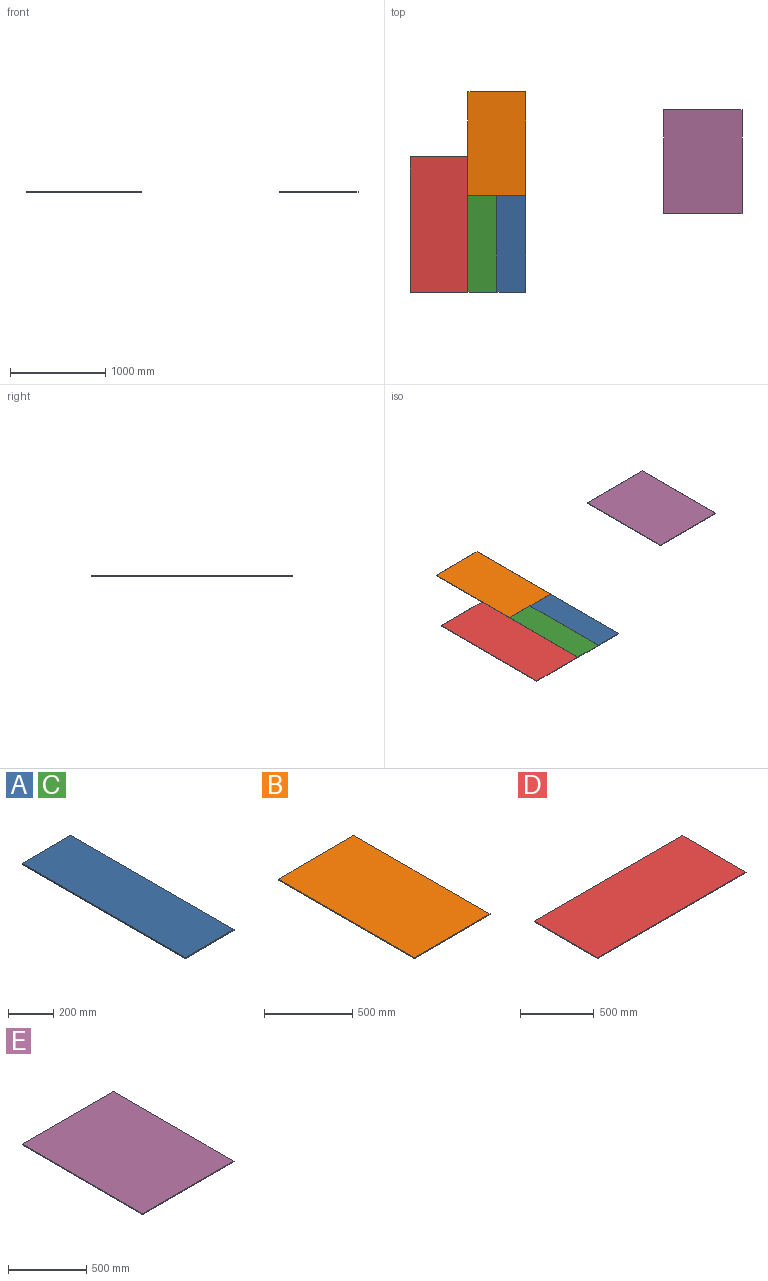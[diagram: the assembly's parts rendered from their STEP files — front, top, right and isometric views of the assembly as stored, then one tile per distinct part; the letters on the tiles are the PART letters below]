
ASSEMBLY  parts=5 mates=10
PART A: 6 faces, bbox 304.8x1016x6.4 mm
  f0: plane 304.8x6.35mm, normal (0,-1,0), area 1935.5mm2, adj f1,f3,f4,f5
  f1: plane 1016x6.35mm, normal (1,0,0), area 6451.6mm2, adj f0,f2,f4,f5
  f2: plane 304.8x6.35mm, normal (0,1,0), area 1935.5mm2, adj f1,f3,f4,f5
  f3: plane 1016x6.35mm, normal (-1,0,0), area 6451.6mm2, adj f0,f2,f4,f5
  f4: plane 1016x304.8mm, normal (0,0,1), area 309676.8mm2, adj f0,f1,f2,f3
  f5: plane 1016x304.8mm, normal (0,0,-1), area 309676.8mm2, adj f0,f1,f2,f3
PART B: 6 faces, bbox 609.6x1092.2x6.4 mm
  f0: plane 609.6x6.35mm, normal (0,-1,0), area 3871mm2, adj f1,f3,f4,f5
  f1: plane 1092.2x6.35mm, normal (1,0,0), area 6935.5mm2, adj f0,f2,f4,f5
  f2: plane 609.6x6.35mm, normal (0,1,0), area 3871mm2, adj f1,f3,f4,f5
  f3: plane 1092.2x6.35mm, normal (-1,0,0), area 6935.5mm2, adj f0,f2,f4,f5
  f4: plane 1092.2x609.6mm, normal (0,0,1), area 665805.1mm2, adj f0,f1,f2,f3
  f5: plane 1092.2x609.6mm, normal (0,0,-1), area 665805.1mm2, adj f0,f1,f2,f3
PART C: same geometry as A
PART D: 6 faces, bbox 1422.4x609.6x6.4 mm
  f0: plane 1422.4x6.35mm, normal (0,-1,0), area 9032.2mm2, adj f1,f3,f4,f5
  f1: plane 609.6x6.35mm, normal (1,0,0), area 3871mm2, adj f0,f2,f4,f5
  f2: plane 1422.4x6.35mm, normal (0,1,0), area 9032.2mm2, adj f1,f3,f4,f5
  f3: plane 609.6x6.35mm, normal (-1,0,0), area 3871mm2, adj f0,f2,f4,f5
  f4: plane 1422.4x609.6mm, normal (0,0,1), area 867095mm2, adj f0,f1,f2,f3
  f5: plane 1422.4x609.6mm, normal (0,0,-1), area 867095mm2, adj f0,f1,f2,f3
PART E: 6 faces, bbox 825.5x1092.2x6.4 mm
  f0: plane 825.5x6.35mm, normal (0,-1,0), area 5241.9mm2, adj f1,f3,f4,f5
  f1: plane 1092.2x6.35mm, normal (1,0,0), area 6935.5mm2, adj f0,f2,f4,f5
  f2: plane 825.5x6.35mm, normal (0,1,0), area 5241.9mm2, adj f1,f3,f4,f5
  f3: plane 1092.2x6.35mm, normal (-1,0,0), area 6935.5mm2, adj f0,f2,f4,f5
  f4: plane 1092.2x825.5mm, normal (0,0,1), area 901611.1mm2, adj f0,f1,f2,f3
  f5: plane 1092.2x825.5mm, normal (0,0,-1), area 901611.1mm2, adj f0,f1,f2,f3
PLACE A t=(-1869.77,-567.26,-3082.5)mm
PLACE B t=(-2174.57,448.74,-3082.5)mm
PLACE C t=(-2174.57,-567.26,-3082.5)mm
PLACE D rot(axis=(0,0,-1),90deg) t=(-2558.21,673.79,-3082.5)mm
PLACE E t=(-118.27,259.39,-3082.5)mm
MATE planar A.f3 <-> C.f1  axis (-1,0,0) through (-1847.47,-262.91,-3079.32)mm
MATE planar C.f0 <-> D.f1  axis (0,-1,0) through (-1999.87,-770.91,-3079.32)mm
MATE planar D.f2 <-> C.f3  axis (1,0,0) through (-2152.27,-59.71,-3079.32)mm
MATE planar E.f4 <-> D.f4  axis (0,0,1) through (316.79,601.84,-3076.15)mm
MATE planar D.f2 <-> B.f3  axis (1,0,0) through (-2152.27,-59.71,-3079.32)mm
MATE planar A.f0 <-> C.f0  axis (0,-1,0) through (-1695.07,-770.91,-3079.32)mm
MATE planar E.f4 <-> B.f4  axis (0,0,1) through (316.79,601.84,-3076.15)mm
MATE planar C.f4 <-> E.f4  axis (0,0,1) through (-1999.87,-262.91,-3076.15)mm
MATE planar B.f0 <-> C.f2  axis (0,-1,0) through (-1847.47,245.09,-3079.32)mm
MATE planar A.f4 <-> C.f4  axis (0,0,1) through (-1695.07,-262.91,-3076.15)mm
